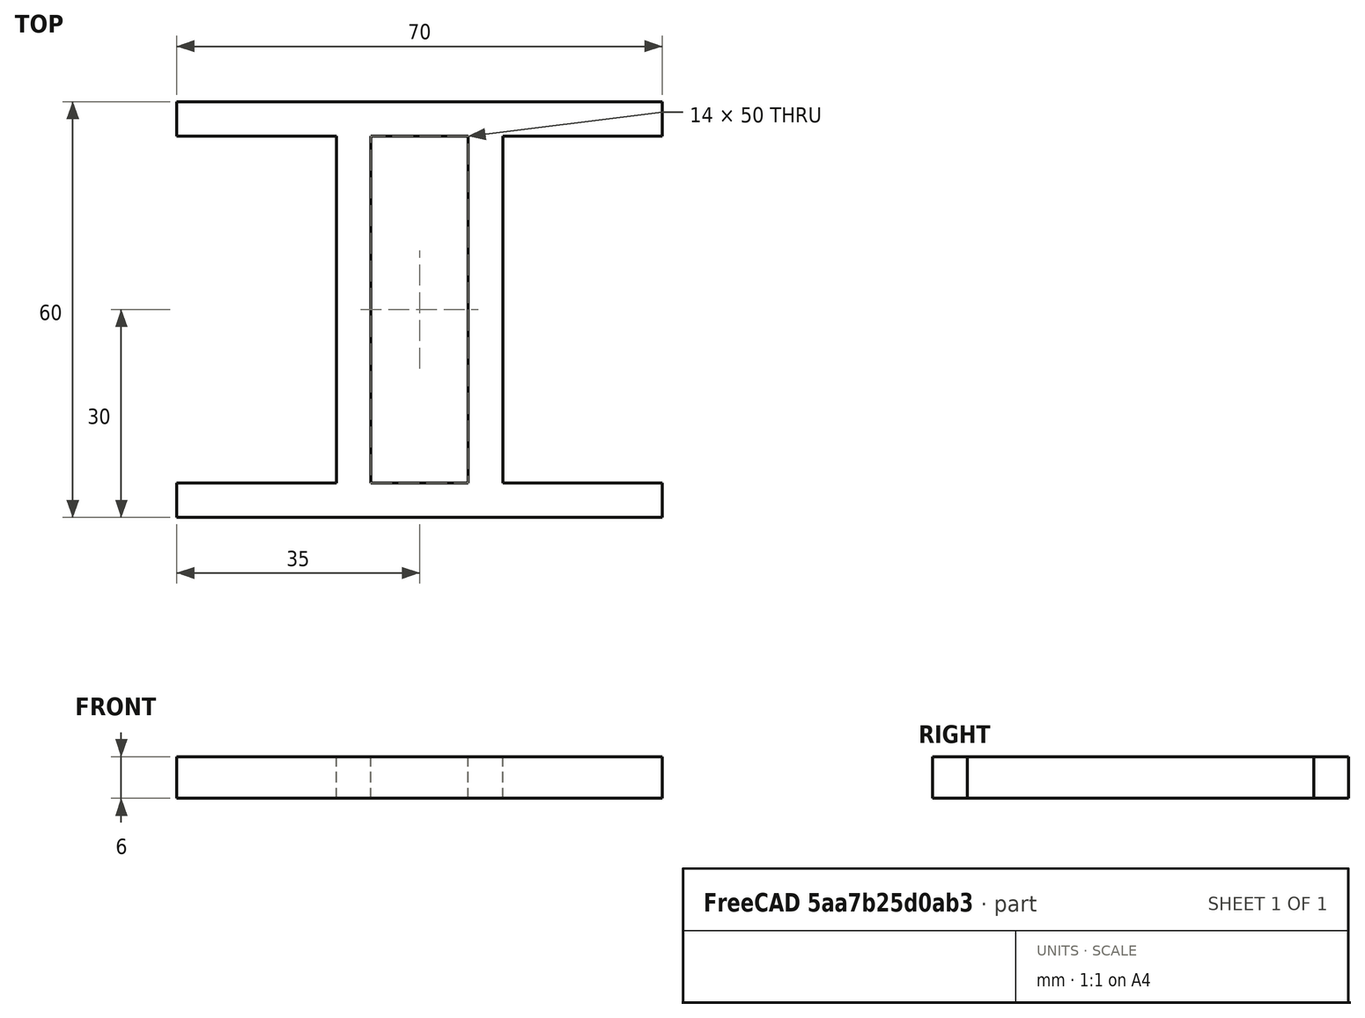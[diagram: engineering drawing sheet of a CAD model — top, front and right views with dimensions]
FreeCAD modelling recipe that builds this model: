
FCSTD DOCUMENT  (FreeCAD 0.14R3702 (Git))
Label: sundial-brace
License: CC-BY 3.0
LicenseURL: http://creativecommons.org/licenses/by/3.0/
objects: Part::Box×4, Part::Cut×3
note: 7 computed .brp shape members not serialized (recipe doc carries the construction recipe); baked Part::Feature solids carry a one-line shape summary decoded from their .brp

FEATURE [Part::Box] Box  label="Cube"
  Height = 6
  Length = 70
  Width = 60
FEATURE [Part::Box] Box001  label="Cube001"
  Height = 10
  Length = 14
  Placement = pos=(28,5,-1) rot=(0,0,1;0rad)
  Width = 50
FEATURE [Part::Box] Box002  label="Cube002"
  Height = 10
  Length = 25
  Placement = pos=(-2,5,-1) rot=(0,0,1;0rad)
  Width = 50
FEATURE [Part::Box] Box003  label="Cube003"
  Height = 10
  Length = 25
  Placement = pos=(47,5,-1) rot=(0,0,1;0rad)
  Width = 50
FEATURE [Part::Cut] Cut
  Base = -> Box
  Tool = -> Box001
FEATURE [Part::Cut] Cut001
  Base = -> Cut
  Tool = -> Box003
FEATURE [Part::Cut] Cut002
  Base = -> Cut001
  Tool = -> Box002
